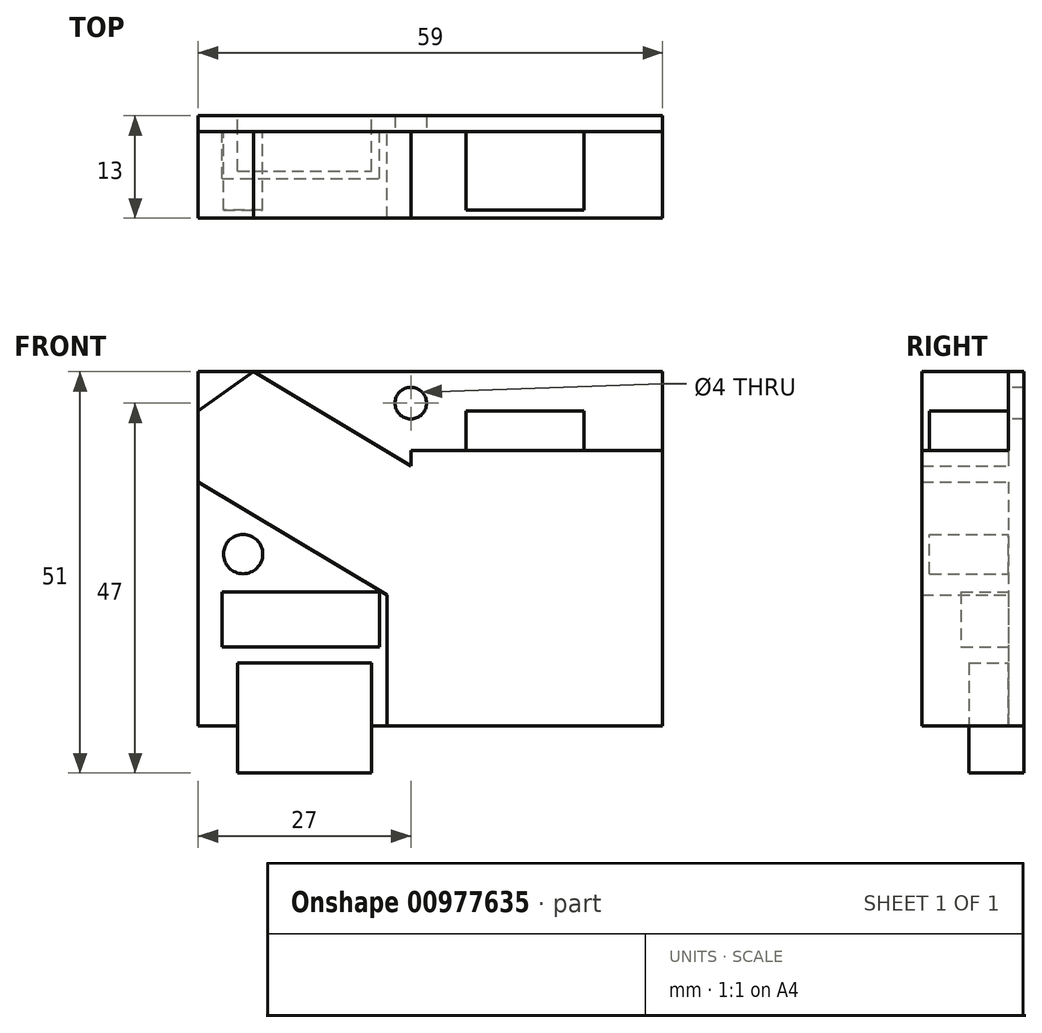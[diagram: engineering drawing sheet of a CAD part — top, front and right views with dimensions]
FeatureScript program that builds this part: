
annotation { "Feature Type Name" : "Feature", "Feature Type Description" : "" }
export const myFeature = defineFeature(function(context is Context, id is Id, definition is map)
    precondition{}
    {
        {
            var Q0;
            Q0=qCreatedBy(makeId("Front.planeOp"),FACE);
            var sketch = newSketch(context, id + "F0", { "sketchPlane" : qUnion([Q0])});
            skLineSegment(sketch, "E0.bottom", {"start": v(-29.5, 22.5) * mm, "end": v(29.5, 22.5) * mm});
            skLineSegment(sketch, "E0.top", {"start": v(-29.5, -22.5) * mm, "end": v(29.5, -22.5) * mm});
            skLineSegment(sketch, "E0.left", {"start": v(-29.5, 22.5) * mm, "end": v(-29.5, -22.5) * mm});
            skLineSegment(sketch, "E0.right", {"start": v(29.5, 22.5) * mm, "end": v(29.5, -22.5) * mm});
            skLineSegment(sketch, "E1.bottom", {"start": v(-24.5, -14.5) * mm, "end": v(-7.5, -14.5) * mm});
            skLineSegment(sketch, "E1.top", {"start": v(-24.5, -28.5) * mm, "end": v(-7.5, -28.5) * mm});
            skLineSegment(sketch, "E1.left", {"start": v(-24.5, -14.5) * mm, "end": v(-24.5, -28.5) * mm});
            skLineSegment(sketch, "E1.right", {"start": v(-7.5, -14.5) * mm, "end": v(-7.5, -28.5) * mm});
            skSolve(sketch);
        }
        {
            var Q0;
            Q0 = qSketchRegion(id + "F0", true);
            extrude(context, id + "F1", {"entities" : qUnion([Q0]), "depth" : 2 * mm, "offsetDistance" : 25 * mm});
        }
        {
            var Q0;
            Q0=makeQuery(id+"F1.opExtrude","CAP_FACE",FACE,{"disambiguationData":[OSD([sQuery(id+"F0.wireOp",EDGE,"E0.bottom"),sQuery(id+"F0.wireOp",EDGE,"E0.top"),sQuery(id+"F0.wireOp",EDGE,"E0.left"),sQuery(id+"F0.wireOp",EDGE,"E0.right")])],"isStart":false});
            var sketch = newSketch(context, id + "F2", { "sketchPlane" : qUnion([Q0])});
            skLineSegment(sketch, "E2.bottom", {"start": v(-5.5, 2.5) * mm, "end": v(29.5, 2.5) * mm});
            skLineSegment(sketch, "E2.top", {"start": v(-5.5, -22.5) * mm, "end": v(29.5, -22.5) * mm});
            skLineSegment(sketch, "E2.left", {"start": v(-5.5, 2.5) * mm, "end": v(-5.5, -22.5) * mm});
            skLineSegment(sketch, "E2.right", {"start": v(29.5, 2.5) * mm, "end": v(29.5, -22.5) * mm});
            skLineSegment(sketch, "E3", {"start": v(-5.5, 12.3) * mm, "end": v(-22.5, 22.5) * mm});
            skLineSegment(sketch, "E4", {"start": v(-22.5, 22.5) * mm, "end": v(-29.5, 17.5) * mm});
            skLineSegment(sketch, "E5", {"start": v(-29.5, 17.5) * mm, "end": v(-29.5, 8.5) * mm});
            skLineSegment(sketch, "E6", {"start": v(-29.5, 8.5) * mm, "end": v(-5.5, -5.9) * mm});
            skLineSegment(sketch, "E7.bottom", {"start": v(-2.5, 12.5) * mm, "end": v(29.5, 12.5) * mm});
            skLineSegment(sketch, "E7.top", {"start": v(-2.5, 2.5) * mm, "end": v(29.5, 2.5) * mm});
            skLineSegment(sketch, "E7.left", {"start": v(-2.5, 12.5) * mm, "end": v(-2.5, 2.5) * mm});
            skLineSegment(sketch, "E7.right", {"start": v(29.5, 12.5) * mm, "end": v(29.5, 2.5) * mm});
            skLineSegment(sketch, "E8", {"start": v(-5.5, 12.3) * mm, "end": v(-2.5, 10.5) * mm});
            skLineSegment(sketch, "E9.bottom", {"start": v(4.5, 17.5) * mm, "end": v(19.5, 17.5) * mm});
            skLineSegment(sketch, "E9.top", {"start": v(4.5, 12.5) * mm, "end": v(19.5, 12.5) * mm});
            skLineSegment(sketch, "E9.left", {"start": v(4.5, 17.5) * mm, "end": v(4.5, 12.5) * mm});
            skLineSegment(sketch, "E9.right", {"start": v(19.5, 17.5) * mm, "end": v(19.5, 12.5) * mm});
            skPoint(sketch, "E10", {"position": v(-2.5, 18.5) * mm});
            skLineSegment(sketch, "E11.bottom", {"start": v(-26.5, -5.5) * mm, "end": v(-6.5, -5.5) * mm});
            skLineSegment(sketch, "E11.top", {"start": v(-26.5, -12.5) * mm, "end": v(-6.5, -12.5) * mm});
            skLineSegment(sketch, "E11.left", {"start": v(-26.5, -5.5) * mm, "end": v(-26.5, -12.5) * mm});
            skLineSegment(sketch, "E11.right", {"start": v(-6.5, -5.5) * mm, "end": v(-6.5, -12.5) * mm});
            skCircle(sketch, "E12", {"center": v(-23.8, -0.68) * mm, "radius": 2.5 * mm});
            skSolve(sketch);
        }
        {
            var Q0;
            {var subQ1=sQuery(id+"F2.wireOp",EDGE,"E2.top");Q0=makeQuery(id+"F2.imprint","IMPRINT",FACE,{"disambiguationData":[TD([[makeQuery(id+"F2.imprint","IMPRINT",EDGE,{"derivedFrom":subQ1}),1.0]])]});}
            var Q1;
            Q1=makeQuery(id+"F2.imprint","IMPRINT",FACE,{"disambiguationData":[TD([[makeQuery(id+"F2.imprint","IMPRINT",EDGE,{"derivedFrom":sQuery(id+"F2.wireOp",EDGE,"E3")}),1.0]])]});
            var Q2;
            {var subQ4=sQuery(id+"F2.wireOp",EDGE,"E7.right");Q2=makeQuery(id+"F2.imprint","IMPRINT",FACE,{"disambiguationData":[TD([[makeQuery(id+"F2.imprint","IMPRINT",EDGE,{"derivedFrom":subQ4}),-1.0]])]});}
            extrude(context, id + "F3", {"entities" : qUnion([Q0, Q1, Q2]), "operationType" : NewBodyOperationType.ADD, "depth" : 11 * mm, "offsetDistance" : 25 * mm});
        }
        {
            var Q0;
            Q0=makeQuery(id+"F2.imprint","IMPRINT",FACE,{"disambiguationData":[TD([[makeQuery(id+"F2.imprint","IMPRINT",EDGE,{"derivedFrom":sQuery(id+"F2.wireOp",EDGE,"E9.bottom")}),-1.0]])]});
            extrude(context, id + "F4", {"entities" : qUnion([Q0]), "operationType" : NewBodyOperationType.ADD, "depth" : 10 * mm, "offsetDistance" : 25 * mm});
        }
        {
            var Q0;
            Q0=sQuery(id+"F2.wireOp",VERTEX,"E10");
            var Q1;
            Q1=makeQuery(id+"F1.opExtrude","SWEPT_BODY",BODY,{"disambiguationData":[OSD([sQuery(id+"F0.wireOp",EDGE,"E0.bottom"),sQuery(id+"F0.wireOp",EDGE,"E0.top"),sQuery(id+"F0.wireOp",EDGE,"E0.left"),sQuery(id+"F0.wireOp",EDGE,"E0.right")])]});
            hole(context, id + "F5", {"style" : HoleStyle.SIMPLE, "endStyle" : HoleEndStyle.BLIND, "holeDiameter" : 4 * mm, "majorDiameter" : 5 * mm, "holeDepth" : 6 * mm, "isTappedThrough" : true, "tappedDepth" : 12 * mm, "tapClearance" : 3, "locations" : qUnion([Q0]), "scope" : qUnion([Q1])});
        }
        {
            var Q0;
            Q0=makeQuery(id+"F2.imprint","IMPRINT",FACE,{"disambiguationData":[TD([[makeQuery(id+"F2.imprint","IMPRINT",EDGE,{"derivedFrom":sQuery(id+"F2.wireOp",EDGE,"E11.bottom")}),-1.0]])]});
            extrude(context, id + "F6", {"entities" : qUnion([Q0]), "operationType" : NewBodyOperationType.ADD, "depth" : 6 * mm, "offsetDistance" : 25 * mm});
        }
        {
            var Q0;
            Q0=makeQuery(id+"F2.imprint","IMPRINT",FACE,{"disambiguationData":[TD([[makeQuery(id+"F2.imprint","IMPRINT",EDGE,{"derivedFrom":sQuery(id+"F2.wireOp",EDGE,"E12")}),1.0]])]});
            extrude(context, id + "F7", {"entities" : qUnion([Q0]), "operationType" : NewBodyOperationType.ADD, "depth" : 10 * mm, "offsetDistance" : 25 * mm});
        }
        {
            var Q0;
            {var subQ5=sQuery(id+"F0.wireOp",EDGE,"E1.top");Q0=makeQuery(id+"F0.imprint","IMPRINT",FACE,{"disambiguationData":[TD([[makeQuery(id+"F0.imprint","IMPRINT",EDGE,{"derivedFrom":subQ5}),1.0]])]});}
            var Q1;
            {var subQ5=sQuery(id+"F0.wireOp",EDGE,"E1.bottom");Q1=makeQuery(id+"F0.imprint","IMPRINT",FACE,{"disambiguationData":[TD([[makeQuery(id+"F0.imprint","IMPRINT",EDGE,{"derivedFrom":subQ5}),-1.0]])]});}
            extrude(context, id + "F8", {"entities" : qUnion([Q0, Q1]), "operationType" : NewBodyOperationType.ADD, "depth" : 7 * mm, "offsetDistance" : 25 * mm});
        }
    });
